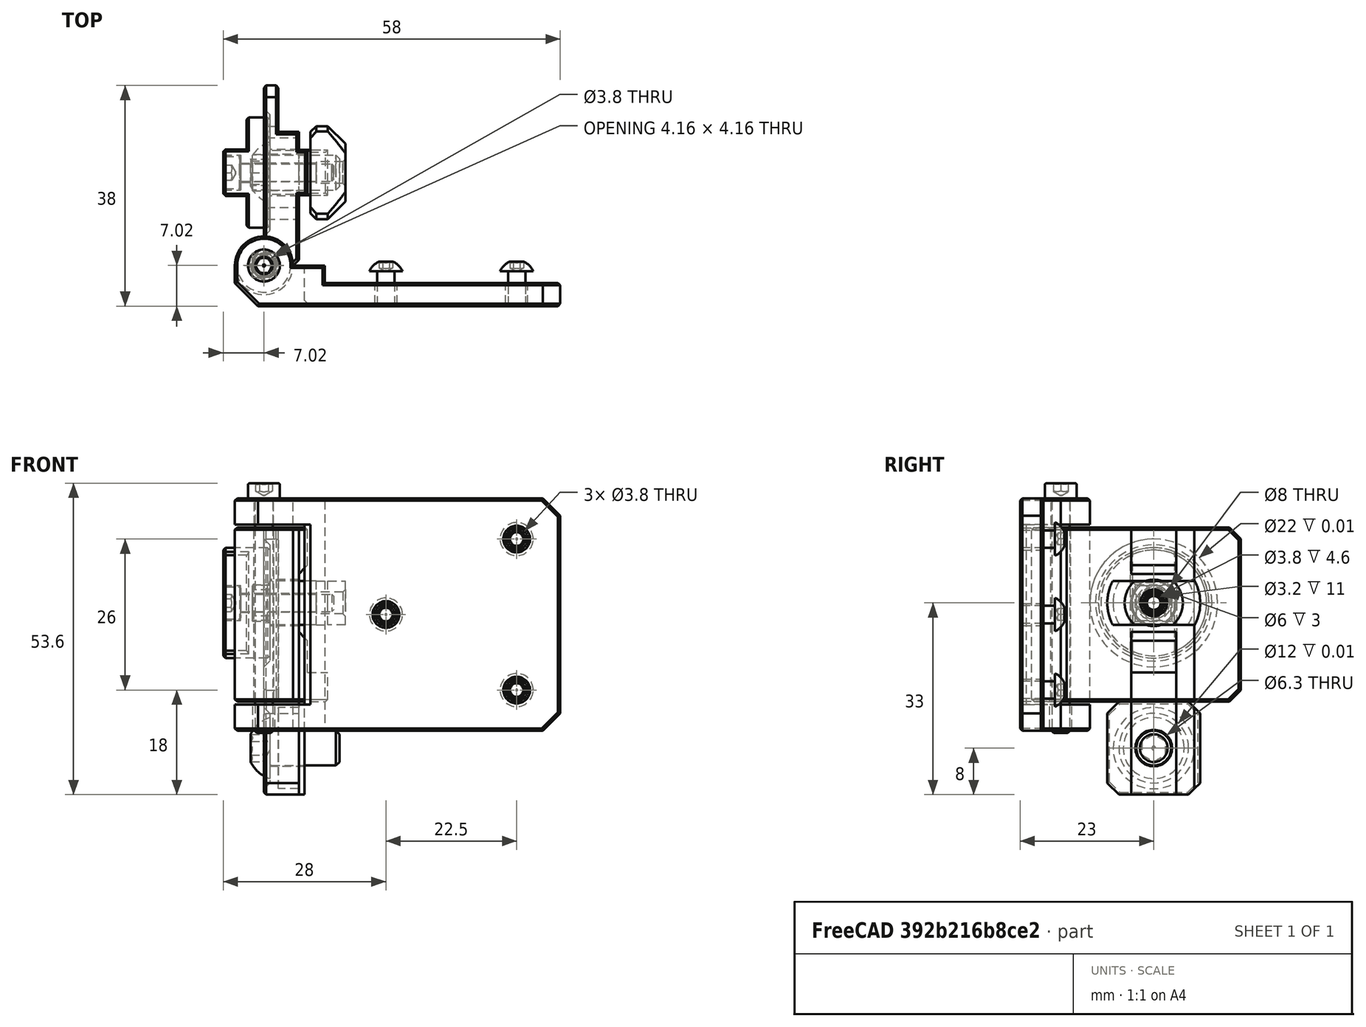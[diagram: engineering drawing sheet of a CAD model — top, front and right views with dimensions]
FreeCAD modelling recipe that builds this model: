
FCSTD DOCUMENT  (FreeCAD 0.19R24291 (Git))
Label: quic-release-door-hinge-assembly
License: Other
LicenseURL: GPL3
objects: Part::FeaturePython×6, Part::Feature×5, App::Part×1
note: 11 computed .brp shape members not serialized (recipe doc carries the construction recipe); baked Part::Feature solids carry a one-line shape summary decoded from their .brp

FEATURE [Part::Feature] Chamfer006006019001
  Placement = pos=(0,0,5) rot=(0,0,1;0rad)
  shape: bbox 16 x 36 x 30 mm, 60 faces (baked)
FEATURE [Part::Feature] Chamfer006006016001
  shape: bbox 8 x 19 x 19 mm, 35 faces (baked)
FEATURE [Part::Feature] Chamfer006006010001
  shape: bbox 56 x 12 x 40 mm, 51 faces (baked)
FEATURE [Part::FeaturePython] Screw  label="M3x16-Screw"  # Fasteners workbench fastener (typed FeaturePython)
  Placement = pos=(-10,15,22) rot=(0,-1,0;1.5708rad)
  baseObject = -> Chamfer006006016001 [Edge61]
  diameter = 4
  invert = true
  length = 6
  lengthCustom = 16
  matchOuter = true
  offset = 0
  thread = false
  type = 33
FEATURE [Part::FeaturePython] Screw001  label="M3x40-Screw"  # Fasteners workbench fastener (typed FeaturePython)
  Placement = pos=(-6,-1,39.6) rot=(0,0,1;0rad)
  baseObject = -> Chamfer006006010001 [Edge71]
  diameter = 4
  invert = false
  length = 10
  lengthCustom = 40
  matchOuter = true
  offset = 0
  thread = false
  type = 33
FEATURE [Part::FeaturePython] Screw002  label="M6x12-Screw"  # Fasteners workbench fastener (typed FeaturePython)
  Placement = pos=(-5,15,-3) rot=(0,-1,0;1.5708rad)
  diameter = 4
  invert = false
  length = 1
  lengthCustom = 12
  matchOuter = true
  offset = 0
  thread = false
  type = 39
FEATURE [Part::FeaturePython] Screw003  label="M3x6-Screw"  # Fasteners workbench fastener (typed FeaturePython)
  Placement = pos=(37.5,-2,33) rot=(-1,0,0;1.5708rad)
  baseObject = -> Chamfer006006010001 [Edge98]
  diameter = 1
  invert = false
  length = 0
  lengthCustom = 6
  matchOuter = true
  offset = 2
  thread = false
  type = 39
FEATURE [Part::FeaturePython] Screw004  label="M3x6-Screw003"  # Fasteners workbench fastener (typed FeaturePython)
  Placement = pos=(37.5,-2,7) rot=(-1,0,0;1.5708rad)
  baseObject = -> Chamfer006006010001 [Edge96]
  diameter = 1
  invert = false
  length = 0
  lengthCustom = 6
  matchOuter = true
  offset = 2
  thread = false
  type = 39
FEATURE [Part::FeaturePython] Screw005  label="M3x6-Screw004"  # Fasteners workbench fastener (typed FeaturePython)
  Placement = pos=(15,-2,20) rot=(-1,0,0;1.5708rad)
  baseObject = -> Chamfer006006010001 [Edge94]
  diameter = 1
  invert = false
  length = 0
  lengthCustom = 6
  matchOuter = true
  offset = 2
  thread = false
  type = 39
FEATURE [Part::Feature] Chamfer006006020001
  shape: bbox 16 x 16 x 12 mm, 35 faces (baked)
FEATURE [Part::Feature] Cut002004005004001
  shape: bbox 7 x 16 x 16 mm, 30 faces (baked)
FEATURE [App::Part] Part  label="door-hinge"
  Group = -> [Chamfer006006019001,Screw,Chamfer006006016001,Screw002,Screw005,Screw004,Screw003,Screw001,Chamfer006006010001,Chamfer006006020001,Cut002004005004001]
  Origin = -> Origin
